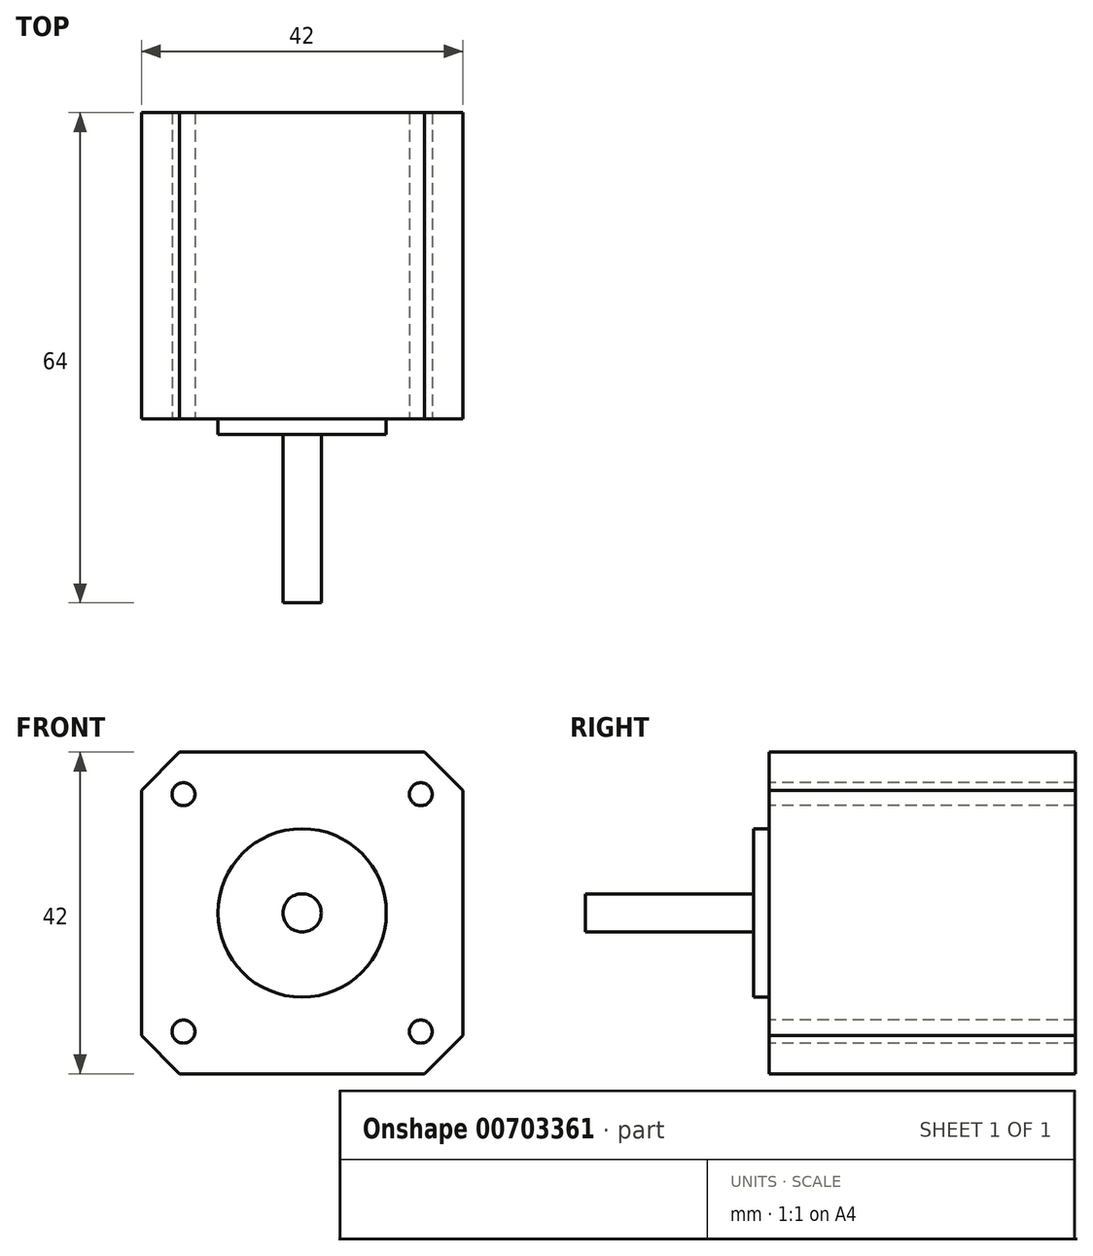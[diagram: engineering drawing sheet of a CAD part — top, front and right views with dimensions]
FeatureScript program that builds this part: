
annotation { "Feature Type Name" : "Feature", "Feature Type Description" : "" }
export const myFeature = defineFeature(function(context is Context, id is Id, definition is map)
    precondition{}
    {
        {
            var Q0;
            Q0=qCreatedBy(makeId("Front.planeOp"),FACE);
            var sketch = newSketch(context, id + "F0", { "sketchPlane" : qUnion([Q0])});
            skCircle(sketch, "E0", {"center": v(0, 0) * mm, "radius": 11 * mm});
            skLineSegment(sketch, "E1.bottom", {"start": v(-21, 21) * mm, "end": v(21, 21) * mm});
            skLineSegment(sketch, "E1.top", {"start": v(-21, -21) * mm, "end": v(21, -21) * mm});
            skLineSegment(sketch, "E1.left", {"start": v(-21, 21) * mm, "end": v(-21, -21) * mm});
            skLineSegment(sketch, "E1.right", {"start": v(21, 21) * mm, "end": v(21, -21) * mm});
            skCircle(sketch, "E2", {"center": v(0, 0) * mm, "radius": 2.5 * mm});
            skLineSegment(sketch, "E3.bottom", {"start": v(-15.5, 15.5) * mm, "end": v(15.5, 15.5) * mm, "construction": true});
            skLineSegment(sketch, "E3.top", {"start": v(-15.5, -15.5) * mm, "end": v(15.5, -15.5) * mm, "construction": true});
            skLineSegment(sketch, "E3.left", {"start": v(-15.5, 15.5) * mm, "end": v(-15.5, -15.5) * mm, "construction": true});
            skLineSegment(sketch, "E3.right", {"start": v(15.5, 15.5) * mm, "end": v(15.5, -15.5) * mm, "construction": true});
            skCircle(sketch, "E4", {"center": v(-15.5, 15.5) * mm, "radius": 1.5 * mm});
            skCircle(sketch, "E5", {"center": v(-15.5, -15.5) * mm, "radius": 1.5 * mm});
            skCircle(sketch, "E6", {"center": v(15.5, -15.5) * mm, "radius": 1.5 * mm});
            skCircle(sketch, "E7", {"center": v(15.5, 15.5) * mm, "radius": 1.5 * mm});
            skSolve(sketch);
        }
        {
            var Q0;
            Q0=makeQuery(id+"F0.imprint","IMPRINT",FACE,{"disambiguationData":[TD([[makeQuery(id+"F0.imprint","IMPRINT",EDGE,{"derivedFrom":sQuery(id+"F0.wireOp",EDGE,"E0")}),-1.0]])]});
            var Q1;
            Q1=makeQuery(id+"F0.imprint","IMPRINT",FACE,{"disambiguationData":[TD([[makeQuery(id+"F0.imprint","IMPRINT",EDGE,{"derivedFrom":sQuery(id+"F0.wireOp",EDGE,"E0")}),1.0]])]});
            var Q2;
            Q2=makeQuery(id+"F0.imprint","IMPRINT",FACE,{"disambiguationData":[TD([[makeQuery(id+"F0.imprint","IMPRINT",EDGE,{"derivedFrom":sQuery(id+"F0.wireOp",EDGE,"E2")}),1.0]])]});
            extrude(context, id + "F1", {"entities" : qUnion([Q0, Q1, Q2]), "oppositeDirection" : true, "depth" : 40 * mm, "offsetDistance" : 25 * mm});
        }
        {
            var Q0;
            Q0=makeQuery(id+"F0.imprint","IMPRINT",FACE,{"disambiguationData":[TD([[makeQuery(id+"F0.imprint","IMPRINT",EDGE,{"derivedFrom":sQuery(id+"F0.wireOp",EDGE,"E0")}),1.0]])]});
            extrude(context, id + "F2", {"entities" : qUnion([Q0]), "operationType" : NewBodyOperationType.ADD, "depth" : 2 * mm, "offsetDistance" : 25 * mm});
        }
        {
            var Q0;
            Q0=makeQuery(id+"F0.imprint","IMPRINT",FACE,{"disambiguationData":[TD([[makeQuery(id+"F0.imprint","IMPRINT",EDGE,{"derivedFrom":sQuery(id+"F0.wireOp",EDGE,"E2")}),1.0]])]});
            extrude(context, id + "F3", {"entities" : qUnion([Q0]), "operationType" : NewBodyOperationType.ADD, "depth" : 24 * mm, "offsetDistance" : 25 * mm});
        }
        {
            var Q0;
            Q0=makeQuery(id+"F1.opExtrude","SWEPT_EDGE",EDGE,{"disambiguationData":[OSD([sQuery(id+"F0.wireOp",EDGE,"E1.top"),sQuery(id+"F0.wireOp",EDGE,"E1.left")])]});
            var Q1;
            Q1=makeQuery(id+"F1.opExtrude","SWEPT_EDGE",EDGE,{"disambiguationData":[OSD([sQuery(id+"F0.wireOp",EDGE,"E1.bottom"),sQuery(id+"F0.wireOp",EDGE,"E1.left")])]});
            var Q2;
            Q2=makeQuery(id+"F1.opExtrude","SWEPT_EDGE",EDGE,{"disambiguationData":[OSD([sQuery(id+"F0.wireOp",EDGE,"E1.bottom"),sQuery(id+"F0.wireOp",EDGE,"E1.right")])]});
            var Q3;
            Q3=makeQuery(id+"F1.opExtrude","SWEPT_EDGE",EDGE,{"disambiguationData":[OSD([sQuery(id+"F0.wireOp",EDGE,"E1.top"),sQuery(id+"F0.wireOp",EDGE,"E1.right")])]});
            chamfer(context, id + "F4", {"entities" : qUnion([Q0, Q1, Q2, Q3]), "width" : 5 * mm, "tangentPropagation" : true});
        }
    });
